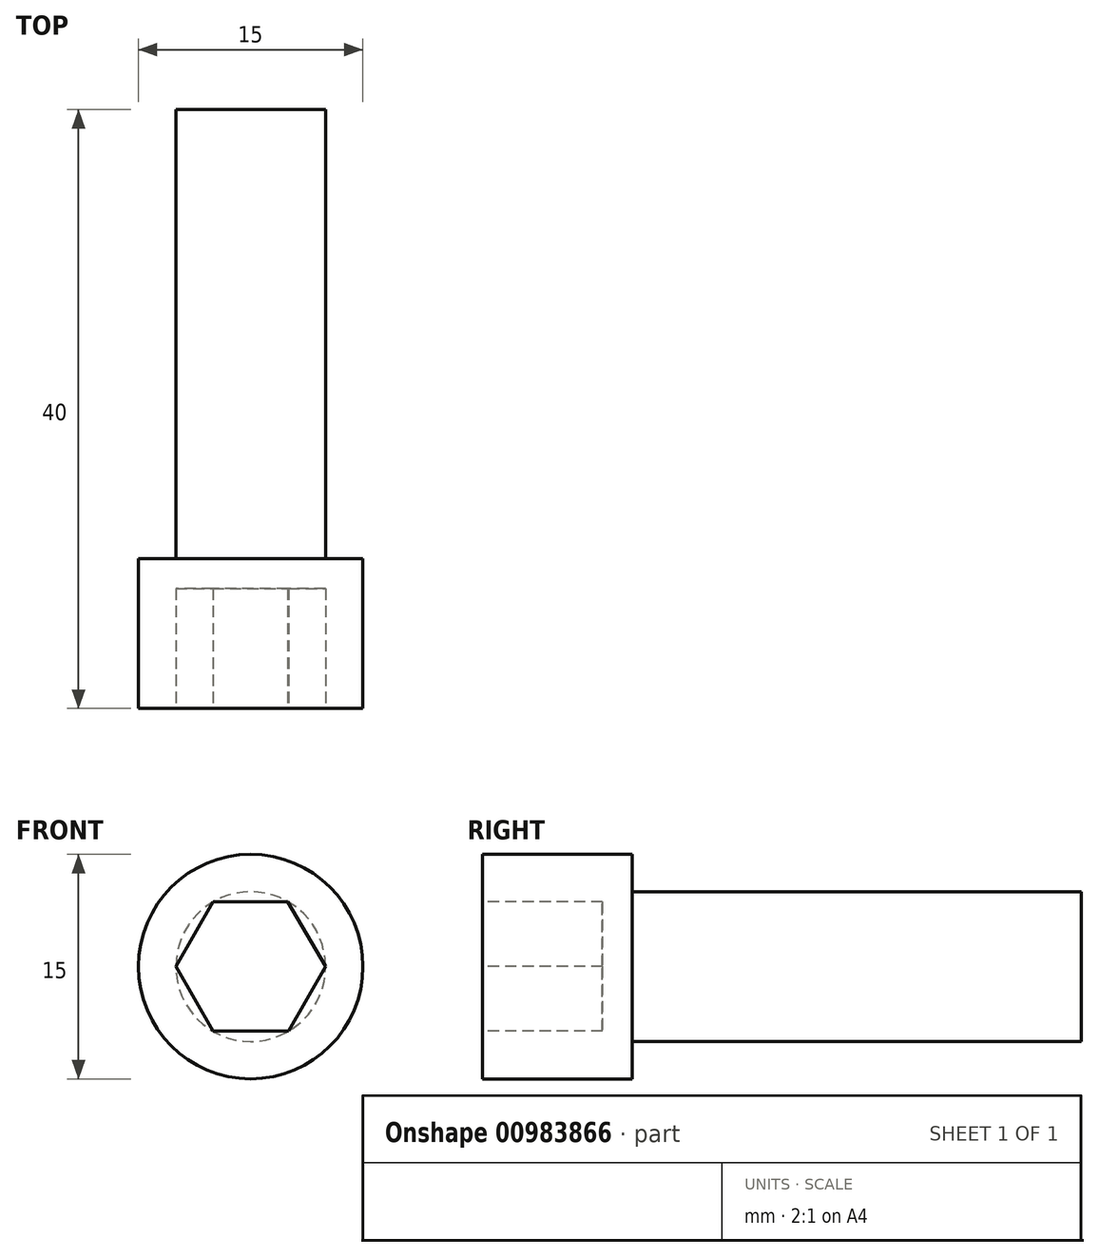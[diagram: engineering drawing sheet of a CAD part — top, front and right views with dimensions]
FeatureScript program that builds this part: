
annotation { "Feature Type Name" : "Feature", "Feature Type Description" : "" }
export const myFeature = defineFeature(function(context is Context, id is Id, definition is map)
    precondition{}
    {
        {
            var Q0;
            Q0=qCreatedBy(makeId("Front.planeOp"),FACE);
            var sketch = newSketch(context, id + "F0", { "sketchPlane" : qUnion([Q0])});
            skCircle(sketch, "E0", {"center": v(0, 0) * mm, "radius": 5 * mm});
            skSolve(sketch);
        }
        {
            var Q0;
            Q0=makeQuery(id+"F0.imprint","IMPRINT",FACE,{"disambiguationData":[TD([[makeQuery(id+"F0.imprint","IMPRINT",EDGE,{"derivedFrom":sQuery(id+"F0.wireOp",EDGE,"E0")}),1.0]])]});
            extrude(context, id + "F1", {"entities" : qUnion([Q0]), "oppositeDirection" : true, "depth" : 30 * mm, "offsetDistance" : 25 * mm});
        }
        {
            var Q0;
            Q0=makeQuery(id+"F1.opExtrude","CAP_FACE",FACE,{"disambiguationData":[OSD([sQuery(id+"F0.wireOp",EDGE,"E0")])],"isStart":true});
            cPlane(context, id + "F2", {"entities" : qUnion([Q0]), "cplaneType" : CPlaneType.OFFSET, "offset" : 0 * mm, "width" : 150 * mm, "height" : 150 * mm});
        }
        {
            var Q0;
            Q0=qCreatedBy(id+"F2.planeOp",FACE);
            var sketch = newSketch(context, id + "F3", { "sketchPlane" : qUnion([Q0])});
            skCircle(sketch, "E1", {"center": v(0, 0) * mm, "radius": 7.5 * mm});
            skSolve(sketch);
        }
        {
            var Q0;
            Q0=makeQuery(id+"F3.imprint","IMPRINT",FACE,{"disambiguationData":[TD([[makeQuery(id+"F3.imprint","IMPRINT",EDGE,{"derivedFrom":sQuery(id+"F3.wireOp",EDGE,"E1")}),1.0]])]});
            extrude(context, id + "F4", {"entities" : qUnion([Q0]), "operationType" : NewBodyOperationType.ADD, "depth" : 10 * mm, "offsetDistance" : 25 * mm});
        }
        {
            var Q0;
            Q0=makeQuery(id+"F4.opExtrude","CAP_FACE",FACE,{"disambiguationData":[OSD([sQuery(id+"F3.wireOp",EDGE,"E1")])],"isStart":false});
            cPlane(context, id + "F5", {"entities" : qUnion([Q0]), "cplaneType" : CPlaneType.OFFSET, "offset" : 0 * mm, "width" : 150 * mm, "height" : 150 * mm});
        }
        {
            var Q0;
            Q0=qCreatedBy(id+"F5.planeOp",FACE);
            var sketch = newSketch(context, id + "F6", { "sketchPlane" : qUnion([Q0])});
            skPoint(sketch, "E2.MirrorCS.start.orphan", {"position": v(0, 0) * mm});
            skLineSegment(sketch, "E3", {"start": v(2.48, 4.34) * mm, "end": v(-2.52, 4.32) * mm});
            skLineSegment(sketch, "E4", {"start": v(-2.52, 4.32) * mm, "end": v(-5, 0) * mm});
            skLineSegment(sketch, "E5", {"start": v(-5, 0) * mm, "end": v(-2.53, -4.31) * mm});
            skLineSegment(sketch, "E6", {"start": v(-2.53, -4.31) * mm, "end": v(2.53, -4.31) * mm});
            skLineSegment(sketch, "E7", {"start": v(2.53, -4.31) * mm, "end": v(5, 0) * mm});
            skLineSegment(sketch, "E8", {"start": v(5, 0) * mm, "end": v(2.48, 4.34) * mm});
            skSolve(sketch);
        }
        {
            var Q0;
            Q0=makeQuery(id+"F6.imprint","IMPRINT",FACE,{"disambiguationData":[TD([[makeQuery(id+"F6.imprint","IMPRINT",EDGE,{"derivedFrom":sQuery(id+"F6.wireOp",EDGE,"tIf9LMis-HDvS-PWVP-Jnf2-pe4F5k7qR9kT")}),-1.0]])]});
            var Q1;
            Q1=makeQuery(id+"F6.imprint","IMPRINT",FACE,{"disambiguationData":[TD([[makeQuery(id+"F6.imprint","IMPRINT",EDGE,{"derivedFrom":sQuery(id+"F6.wireOp",EDGE,"E3")}),1.0]])]});
            extrude(context, id + "F7", {"entities" : qUnion([Q0, Q1]), "operationType" : NewBodyOperationType.REMOVE, "oppositeDirection" : true, "depth" : 8 * mm, "offsetDistance" : 25 * mm});
        }
    });
